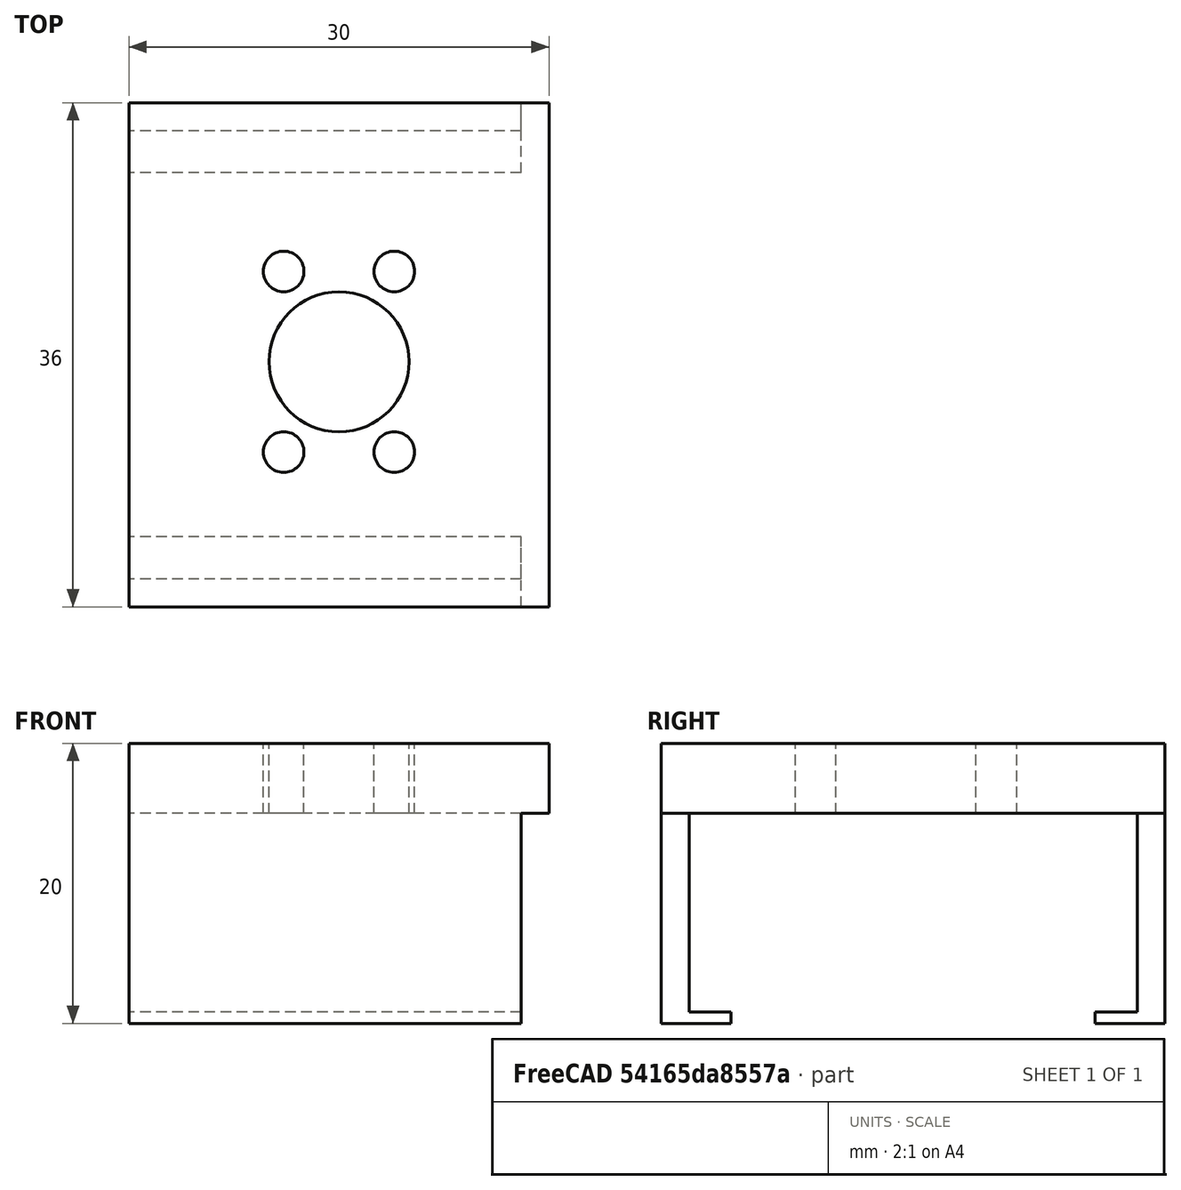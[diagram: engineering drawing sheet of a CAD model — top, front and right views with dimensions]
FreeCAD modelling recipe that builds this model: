
FCSTD DOCUMENT  (FreeCAD 0.16R6712 (Git))
Label: tornillosinfin
License: All rights reserved
LicenseURL: http://en.wikipedia.org/wiki/All_rights_reserved
objects: Part::Box×5, Part::Cylinder×2, Part::Cut×2, Part::MultiFuse×1, Part::FeaturePython×1, Part::Feature×1
note: 12 computed .brp shape members not serialized (recipe doc carries the construction recipe); baked Part::Feature solids carry a one-line shape summary decoded from their .brp

FEATURE [Part::Box] Box  label="Cubo"
  Height = 5
  Length = 30
  Placement = pos=(0,0,15) rot=(0,0,1;0rad)
  Width = 36
FEATURE [Part::Box] Box001  label="Cubo001"
  Height = 15
  Length = 2
  Placement = pos=(28,34,0) rot=(0,0,1;1.5708rad)
  Width = 28
FEATURE [Part::Box] Box002  label="Cubo002"
  Height = 15
  Length = 2
  Placement = pos=(28,0,0) rot=(0,0,1;1.5708rad)
  Width = 28
FEATURE [Part::Box] Box003  label="Cubo003"
  Height = 0.8
  Length = 3
  Placement = pos=(28,31,0) rot=(0,0,1;1.5708rad)
  Width = 28
FEATURE [Part::Box] Box004  label="Cubo004"
  Height = 0.8
  Length = 3
  Placement = pos=(28,2,0) rot=(0,0,1;1.5708rad)
  Width = 28
FEATURE [Part::Cylinder] Cylinder  label="Cilindro"
  Angle = 360
  Height = 10
  Placement = pos=(15,17.5,10) rot=(0,0,1;0rad)
  Radius = 5
FEATURE [Part::MultiFuse] Fusion
  Shapes = -> [Box,Box001,Box002,Box003,Box004]
FEATURE [Part::Cut] Cut
  Base = -> Fusion
  Tool = -> Cylinder
FEATURE [Part::Cylinder] Cylinder002  label="Cilindro002"
  Angle = 360
  Height = 10
  Placement = pos=(9,19,10) rot=(0,0,1;0rad)
  Radius = 1.45
FEATURE [Part::FeaturePython] Array  # Draft array (typed FeaturePython)
  Angle = 360
  ArrayType = 0
  Axis = (0,0,1)
  Base = -> Cylinder002
  Center = (0,0,0)
  Fuse = false
  IntervalAxis = (0,0,0)
  IntervalX = (7.9,0,0)
  IntervalY = (0,-12.9,0)
  IntervalZ = (0,0,0)
  NumberPolar = 1
  NumberX = 2
  NumberY = 2
  NumberZ = 1
  Placement = pos=(2.05,4.95,0) rot=(0,0,1;0rad)
FEATURE [Part::Cut] Cut001
  Base = -> Cut
  Tool = -> Array
FEATURE [Part::Feature] Cut001001  label="Cut002"
  shape: bbox 30 x 36 x 20 mm, 21 faces (baked)
